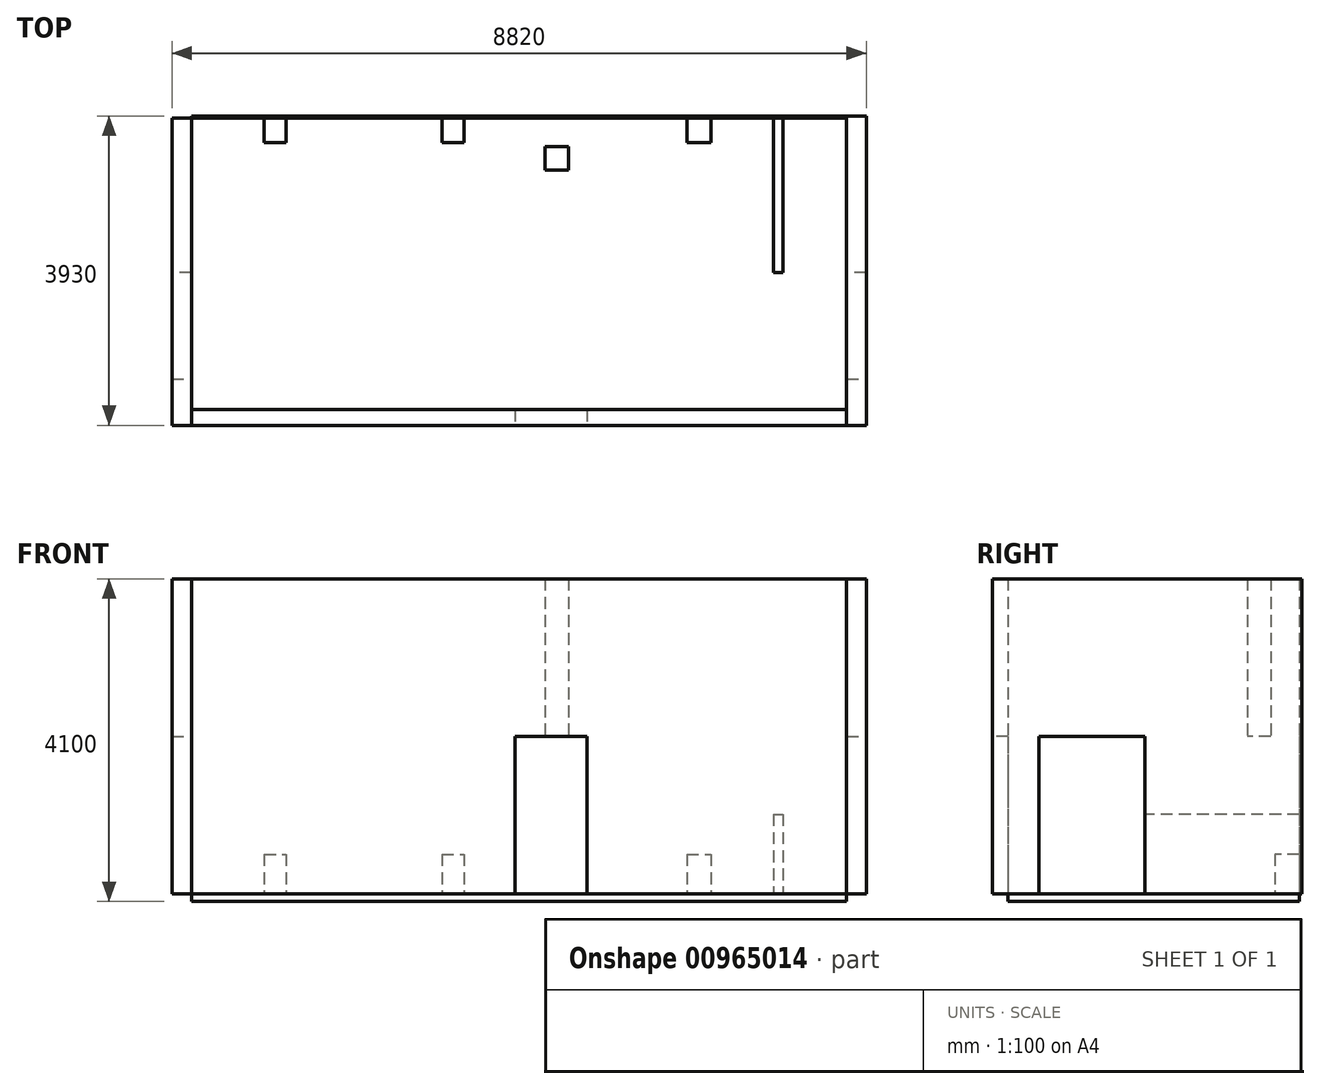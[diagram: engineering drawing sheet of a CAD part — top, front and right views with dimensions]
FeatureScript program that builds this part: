
annotation { "Feature Type Name" : "Feature", "Feature Type Description" : "" }
export const myFeature = defineFeature(function(context is Context, id is Id, definition is map)
    precondition{}
    {
        {
            assignVariable(context, id + "F0", {"variableType" : VariableType.LENGTH, "name" : "visina", "lengthValue" : 4000 * mm});
        }
        {
            var Q0;
            Q0=qCreatedBy(makeId("Top.planeOp"),FACE);
            var sketch = newSketch(context, id + "F1", { "sketchPlane" : qUnion([Q0])});
            skLineSegment(sketch, "E0.bottom", {"start": v(-4160, 1850) * mm, "end": v(4160, 1850) * mm});
            skLineSegment(sketch, "E0.top", {"start": v(-4160, -1850) * mm, "end": v(4160, -1850) * mm});
            skLineSegment(sketch, "E0.left", {"start": v(-4160, 1850) * mm, "end": v(-4160, -1850) * mm});
            skLineSegment(sketch, "E0.right", {"start": v(4160, 1850) * mm, "end": v(4160, -1850) * mm});
            skPoint(sketch, "E0.middle", {"position": v(0, 0) * mm});
            skSolve(sketch);
        }
        {
            var Q0;
            Q0=makeQuery(id+"F1.imprint","IMPRINT",FACE,{"disambiguationData":[TD([[makeQuery(id+"F1.imprint","IMPRINT",EDGE,{"derivedFrom":sQuery(id+"F1.wireOp",EDGE,"E0.bottom")}),-1.0]])]});
            extrude(context, id + "F2", {"entities" : qUnion([Q0]), "oppositeDirection" : true, "depth" : 100 * mm, "offsetDistance" : 25 * mm});
        }
        {
            var Q0;
            Q0=makeQuery(id+"F2.opExtrude","CAP_FACE",FACE,{"disambiguationData":[OSD([sQuery(id+"F1.wireOp",EDGE,"E0.bottom"),sQuery(id+"F1.wireOp",EDGE,"E0.top"),sQuery(id+"F1.wireOp",EDGE,"E0.left"),sQuery(id+"F1.wireOp",EDGE,"E0.right")])],"isStart":true});
            var sketch = newSketch(context, id + "F3", { "sketchPlane" : qUnion([Q0])});
            skLineSegment(sketch, "E1.bottom", {"start": v(330, 1490) * mm, "end": v(630, 1490) * mm});
            skLineSegment(sketch, "E1.top", {"start": v(330, 1190) * mm, "end": v(630, 1190) * mm});
            skLineSegment(sketch, "E1.left", {"start": v(330, 1490) * mm, "end": v(330, 1190) * mm});
            skLineSegment(sketch, "E1.right", {"start": v(630, 1490) * mm, "end": v(630, 1190) * mm});
            skLineSegment(sketch, "E2.bottom", {"start": v(-3240, 1850) * mm, "end": v(-2960, 1850) * mm});
            skLineSegment(sketch, "E2.top", {"start": v(-3240, 1540) * mm, "end": v(-2960, 1540) * mm});
            skLineSegment(sketch, "E2.left", {"start": v(-3240, 1850) * mm, "end": v(-3240, 1540) * mm});
            skLineSegment(sketch, "E2.right", {"start": v(-2960, 1850) * mm, "end": v(-2960, 1540) * mm});
            skLineSegment(sketch, "E3.bottom", {"start": v(-980, 1850) * mm, "end": v(-700, 1850) * mm});
            skLineSegment(sketch, "E3.top", {"start": v(-980, 1540) * mm, "end": v(-700, 1540) * mm});
            skLineSegment(sketch, "E3.left", {"start": v(-980, 1850) * mm, "end": v(-980, 1540) * mm});
            skLineSegment(sketch, "E3.right", {"start": v(-700, 1850) * mm, "end": v(-700, 1540) * mm});
            skLineSegment(sketch, "E4.bottom", {"start": v(3230, 1850) * mm, "end": v(3350, 1850) * mm});
            skLineSegment(sketch, "E4.top", {"start": v(3230, -550) * mm, "end": v(3350, -550) * mm});
            skLineSegment(sketch, "E4.left", {"start": v(3230, 1850) * mm, "end": v(3230, -550) * mm});
            skLineSegment(sketch, "E4.right", {"start": v(3350, 1850) * mm, "end": v(3350, -550) * mm});
            skLineSegment(sketch, "E5.bottom", {"start": v(2130, 1850) * mm, "end": v(2440, 1850) * mm});
            skLineSegment(sketch, "E5.top", {"start": v(2130, 1540) * mm, "end": v(2440, 1540) * mm});
            skLineSegment(sketch, "E5.left", {"start": v(2130, 1850) * mm, "end": v(2130, 1540) * mm});
            skLineSegment(sketch, "E5.right", {"start": v(2440, 1850) * mm, "end": v(2440, 1540) * mm});
            skLineSegment(sketch, "E6.bottom", {"start": v(330.24, 1850) * mm, "end": v(640.24, 1850) * mm});
            skLineSegment(sketch, "E6.top", {"start": v(330.24, 1540) * mm, "end": v(640.24, 1540) * mm});
            skLineSegment(sketch, "E6.left", {"start": v(330.24, 1850) * mm, "end": v(330.24, 1540) * mm});
            skLineSegment(sketch, "E6.right", {"start": v(640.24, 1850) * mm, "end": v(640.24, 1540) * mm});
            skLineSegment(sketch, "E7", {"start": v(4160, -1850) * mm, "end": v(-4160, -1850) * mm});
            skSolve(sketch);
        }
        {
            var Q0;
            Q0=makeQuery(id+"F3.imprint","IMPRINT",FACE,{"disambiguationData":[TD([[makeQuery(id+"F3.imprint","IMPRINT",EDGE,{"derivedFrom":sQuery(id+"F3.wireOp",EDGE,"E1.bottom")}),-1.0]])]});
            extrude(context, id + "F4", {"entities" : qUnion([Q0]), "operationType" : NewBodyOperationType.ADD, "depth" : getVariable(context, 'visina'), "offsetDistance" : 25 * mm});
        }
        {
            var Q0;
            Q0=makeQuery(id+"F3.imprint","IMPRINT",FACE,{"disambiguationData":[TD([[makeQuery(id+"F3.imprint","IMPRINT",EDGE,{"derivedFrom":sQuery(id+"F3.wireOp",EDGE,"E2.bottom")}),-1.0]])]});
            var Q1;
            Q1=makeQuery(id+"F3.imprint","IMPRINT",FACE,{"disambiguationData":[TD([[makeQuery(id+"F3.imprint","IMPRINT",EDGE,{"derivedFrom":sQuery(id+"F3.wireOp",EDGE,"E3.bottom")}),-1.0]])]});
            var Q2;
            Q2=makeQuery(id+"F3.imprint","IMPRINT",FACE,{"disambiguationData":[TD([[makeQuery(id+"F3.imprint","IMPRINT",EDGE,{"derivedFrom":sQuery(id+"F3.wireOp",EDGE,"E5.bottom")}),-1.0]])]});
            var Q3;
            Q3=makeQuery(id+"F3.imprint","IMPRINT",FACE,{"disambiguationData":[TD([[makeQuery(id+"F3.imprint","IMPRINT",EDGE,{"derivedFrom":sQuery(id+"F3.wireOp",EDGE,"E6.bottom")}),-1.0]])]});
            extrude(context, id + "F5", {"entities" : qUnion([Q0, Q1, Q2, Q3]), "operationType" : NewBodyOperationType.ADD, "depth" : 500 * mm, "offsetDistance" : 25 * mm});
        }
        {
            var Q0;
            Q0=makeQuery(id+"F3.imprint","IMPRINT",FACE,{"disambiguationData":[TD([[makeQuery(id+"F3.imprint","IMPRINT",EDGE,{"derivedFrom":sQuery(id+"F3.wireOp",EDGE,"E4.bottom")}),-1.0]])]});
            extrude(context, id + "F6", {"entities" : qUnion([Q0]), "operationType" : NewBodyOperationType.ADD, "depth" : 1010 * mm, "offsetDistance" : 25 * mm});
        }
        {
            var Q0;
            Q0=makeQuery(id+"F2.opExtrude","CAP_FACE",FACE,{"disambiguationData":[OSD([sQuery(id+"F1.wireOp",EDGE,"E0.bottom"),sQuery(id+"F1.wireOp",EDGE,"E0.top"),sQuery(id+"F1.wireOp",EDGE,"E0.left"),sQuery(id+"F1.wireOp",EDGE,"E0.right")])],"isStart":true});
            var sketch = newSketch(context, id + "F7", { "sketchPlane" : qUnion([Q0])});
            skLineSegment(sketch, "E8.bottom", {"start": v(-4160, 1850) * mm, "end": v(4160, 1850) * mm});
            skLineSegment(sketch, "E8.top", {"start": v(-4160, 1880) * mm, "end": v(4160, 1880) * mm});
            skLineSegment(sketch, "E8.left", {"start": v(-4160, 1850) * mm, "end": v(-4160, 1880) * mm});
            skLineSegment(sketch, "E8.right", {"start": v(4160, 1850) * mm, "end": v(4160, 1880) * mm});
            skLineSegment(sketch, "E9.bottom", {"start": v(-4160, 1850) * mm, "end": v(-4410, 1850) * mm});
            skLineSegment(sketch, "E9.top", {"start": v(-4160, -2050) * mm, "end": v(-4410, -2050) * mm});
            skLineSegment(sketch, "E9.left", {"start": v(-4160, 1850) * mm, "end": v(-4160, -2050) * mm});
            skLineSegment(sketch, "E9.right", {"start": v(-4410, 1850) * mm, "end": v(-4410, -2050) * mm});
            skLineSegment(sketch, "E10.bottom", {"start": v(-4160, -1850) * mm, "end": v(4160, -1850) * mm});
            skLineSegment(sketch, "E10.top", {"start": v(-4160, -2050) * mm, "end": v(4160, -2050) * mm});
            skLineSegment(sketch, "E10.left", {"start": v(-4160, -1850) * mm, "end": v(-4160, -2050) * mm});
            skLineSegment(sketch, "E10.right", {"start": v(4160, -1850) * mm, "end": v(4160, -2050) * mm});
            skLineSegment(sketch, "E11.bottom", {"start": v(4160, 1880) * mm, "end": v(4410, 1880) * mm});
            skLineSegment(sketch, "E11.top", {"start": v(4160, -2050) * mm, "end": v(4410, -2050) * mm});
            skLineSegment(sketch, "E11.left", {"start": v(4160, 1880) * mm, "end": v(4160, -2050) * mm});
            skLineSegment(sketch, "E11.right", {"start": v(4410, 1880) * mm, "end": v(4410, -2050) * mm});
            skSolve(sketch);
        }
        {
            var Q0;
            Q0=makeQuery(id+"F7.imprint","IMPRINT",FACE,{"disambiguationData":[TD([[makeQuery(id+"F7.imprint","IMPRINT",EDGE,{"derivedFrom":sQuery(id+"F7.wireOp",EDGE,"E8.top")}),-1.0]])]});
            extrude(context, id + "F8", {"entities" : qUnion([Q0]), "depth" : getVariable(context, 'visina'), "offsetDistance" : 25 * mm});
        }
        {
            var Q0;
            {var subQ2=sQuery(id+"F7.wireOp",EDGE,"E11.bottom");Q0=makeQuery(id+"F7.imprint","IMPRINT",FACE,{"disambiguationData":[TD([[makeQuery(id+"F7.imprint","IMPRINT",EDGE,{"derivedFrom":subQ2}),-1.0]])]});}
            extrude(context, id + "F9", {"entities" : qUnion([Q0]), "depth" : getVariable(context, 'visina'), "offsetDistance" : 25 * mm});
        }
        {
            var Q0;
            Q0=makeQuery(id+"F7.imprint","IMPRINT",FACE,{"disambiguationData":[TD([[makeQuery(id+"F7.imprint","IMPRINT",EDGE,{"derivedFrom":sQuery(id+"F7.wireOp",EDGE,"E9.bottom")}),1.0]])]});
            extrude(context, id + "F10", {"entities" : qUnion([Q0]), "depth" : getVariable(context, 'visina'), "offsetDistance" : 25 * mm});
        }
        {
            var Q0;
            {var subQ0=sQuery(id+"F7.wireOp",EDGE,"E10.bottom");Q0=makeQuery(id+"F7.imprint","IMPRINT",FACE,{"disambiguationData":[TD([[makeQuery(id+"F7.imprint","IMPRINT",EDGE,{"derivedFrom":subQ0}),-1.0]])]});}
            extrude(context, id + "F11", {"entities" : qUnion([Q0]), "depth" : getVariable(context, 'visina'), "offsetDistance" : 25 * mm});
        }
        {
            var Q0;
            Q0=makeQuery(id+"F9.opExtrude","SWEPT_FACE",FACE,{"disambiguationData":[OSD([sQuery(id+"F7.wireOp",EDGE,"E11.right")])]});
            var sketch = newSketch(context, id + "F12", { "sketchPlane" : qUnion([Q0])});
            skLineSegment(sketch, "E12.bottom", {"start": v(-1460, 0) * mm, "end": v(-760, 0) * mm});
            skLineSegment(sketch, "E12.top", {"start": v(-1460, 2000) * mm, "end": v(-760, 2000) * mm});
            skLineSegment(sketch, "E12.left", {"start": v(-1460, 0) * mm, "end": v(-1460, 2000) * mm});
            skLineSegment(sketch, "E12.right", {"start": v(-760, 0) * mm, "end": v(-760, 2000) * mm});
            skSolve(sketch);
        }
        {
            var Q0;
            Q0=makeQuery(id+"F12.imprint","IMPRINT",FACE,{"disambiguationData":[TD([[makeQuery(id+"F12.imprint","IMPRINT",EDGE,{"derivedFrom":sQuery(id+"F12.wireOp",EDGE,"E12.bottom")}),-1.0]])]});
            extrude(context, id + "F13", {"entities" : qUnion([Q0]), "operationType" : NewBodyOperationType.REMOVE, "endBound" : BoundingType.THROUGH_ALL, "oppositeDirection" : true, "depth" : 25 * mm, "offsetDistance" : 25 * mm});
        }
        {
            var Q0;
            Q0=makeQuery(id+"F10.opExtrude","SWEPT_FACE",FACE,{"disambiguationData":[OSD([sQuery(id+"F7.wireOp",EDGE,"E9.right")])]});
            var sketch = newSketch(context, id + "F14", { "sketchPlane" : qUnion([Q0])});
            skLineSegment(sketch, "E13.bottom", {"start": v(110, 0) * mm, "end": v(1010, 0) * mm});
            skLineSegment(sketch, "E13.top", {"start": v(110, 2000) * mm, "end": v(1010, 2000) * mm});
            skLineSegment(sketch, "E13.left", {"start": v(110, 0) * mm, "end": v(110, 2000) * mm});
            skLineSegment(sketch, "E13.right", {"start": v(1010, 0) * mm, "end": v(1010, 2000) * mm});
            skSolve(sketch);
        }
        {
            var Q0;
            Q0=makeQuery(id+"F14.imprint","IMPRINT",FACE,{"disambiguationData":[TD([[makeQuery(id+"F14.imprint","IMPRINT",EDGE,{"derivedFrom":sQuery(id+"F14.wireOp",EDGE,"E13.bottom")}),1.0]])]});
            extrude(context, id + "F15", {"entities" : qUnion([Q0]), "operationType" : NewBodyOperationType.REMOVE, "endBound" : BoundingType.THROUGH_ALL, "oppositeDirection" : true, "depth" : 25 * mm, "offsetDistance" : 25 * mm});
        }
        {
            var Q0;
            Q0=makeQuery(id+"F11.opExtrude","SWEPT_FACE",FACE,{"disambiguationData":[OSD([sQuery(id+"F7.wireOp",EDGE,"E10.top")])]});
            var sketch = newSketch(context, id + "F16", { "sketchPlane" : qUnion([Q0])});
            skLineSegment(sketch, "E14.bottom", {"start": v(860, 0) * mm, "end": v(-50, 0) * mm});
            skLineSegment(sketch, "E14.top", {"start": v(860, 2000) * mm, "end": v(-50, 2000) * mm});
            skLineSegment(sketch, "E14.left", {"start": v(860, 0) * mm, "end": v(860, 2000) * mm});
            skLineSegment(sketch, "E14.right", {"start": v(-50, 0) * mm, "end": v(-50, 2000) * mm});
            skSolve(sketch);
        }
        {
            var Q0;
            Q0=makeQuery(id+"F16.imprint","IMPRINT",FACE,{"disambiguationData":[TD([[makeQuery(id+"F16.imprint","IMPRINT",EDGE,{"derivedFrom":sQuery(id+"F16.wireOp",EDGE,"E14.bottom")}),1.0]])]});
            extrude(context, id + "F17", {"entities" : qUnion([Q0]), "operationType" : NewBodyOperationType.REMOVE, "endBound" : BoundingType.THROUGH_ALL, "oppositeDirection" : true, "depth" : 25 * mm, "offsetDistance" : 25 * mm});
        }
    });
